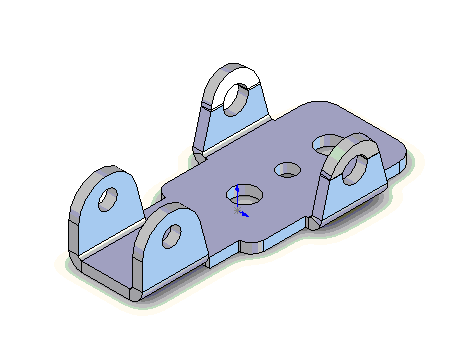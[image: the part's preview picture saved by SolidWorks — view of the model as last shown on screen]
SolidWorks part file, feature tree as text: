
SOLIDWORKS PART (.sldprt)
format: sldprt  version: not decoded by parser v0  size: 605,184 bytes
history: native  units: mm
features: sketch x7, cut_extrude x3, fillet x2, extrude x1, shell x1, sheet_metal_op x1 (+11 scaffold rows collapsed)
feature tree (26):
  scaffold x11  (default folders/planes/origin — collapsed)
  sketch  "Sketch1"  dims[D1=42.8625mm D2=21.0mm]
  extrude  "Extrude1"  Depth=11.1125mm
  sketch  "Sketch2"  dims[c1.D9=2.0mm c1.D10=1.0mm c1.D11=4.2mm c1.D12=4.1mm c1.D13=4.1mm c1.D7=3.0mm c1.D1=2.5mm c1.D2=4.5mm c1.D3=2.0mm c2.D3=95.0deg c2.D4=~2.645638mm c3.D4=100.0deg c3.D5=~2.839605mm c4.D5=100.0deg c4.D6=11.0mm c4.D7=7.9mm c4.D8=16.0mm c4.D12=14.0mm c4.D13=6.2mm c5.D5=6.5405mm c5.D14=7.0mm]
  cut_extrude  "Cut-Extrude1"  [1 undecoded]
  fillet  "Fillet1"  Radius=0.25mm
  sketch  "Sketch3"  dims[c1.D2=~3.061489mm c1.D3=~3.061489mm c1.D4=~3.061489mm c1.D5=8.0mm c1.D6=4.1mm c1.D8=3.1mm c2.D4=3.1mm c2.D9=4.1mm c2.D1=1.6mm c2.D2=10.7mm c2.D3=~7.79288mm c3.D2=7.62mm c3.D3=4.7625mm c3.D4=26.0mm c3.D7=~5.455429mm c4.D7=75.0deg c4.D4=~24.912848mm c4.D9=6.7mm c5.D4=25.4mm c5.D3=1.27mm]
  cut_extrude  "Cut-Extrude2"  [1 undecoded]
  sketch  "Sketch6"  dims[c1.D1=1.0mm c1.D2=1.0mm c2.D1=2.0mm c2.D2=3.0mm c2.D3=~2.895126mm c3.D3=100.0deg c3.D4=~2.519283mm c4.D4=100.0deg]
  cut_extrude  "Cut-Extrude3"  Depth=20mm
  fillet  "Fillet2"  Radius=3mm
  shell  "Shell2"  Thickness=1.6mm
  sheet_metal_op  "Sheet-Metal2"  Thickness=1.6mm
  sketch  "Sharp-Sketch2"  dims[c1.SharpBend5=0.0 c1.D1=0.0mm c1.D4=90.0deg c1.D5=4.0 c1.D8=0.0mm c1.D9=0.0mm c1.SharpBend6=0.0 c2.D1=0.0mm c2.D4=90.0deg c2.D5=3.0 c2.D8=0.0mm c2.D9=0.0mm c2.SharpBend7=0.0 c3.D1=0.0mm c3.D4=90.0deg c3.D5=2.0 c3.D8=0.0mm c3.D9=0.0mm c4.D1=0.5mm c4.D2=500.0mm c4.D3=0.0mm c5.D2=500.0mm c5.D3=0.0mm c5.D4=90.0deg c5.D5=1.0 c5.D8=0.0mm c5.D9=0.0mm]
  sketch  "Flat-Sketch2"  dims[c1.D1=1.0mm c1.D2=1.0mm c2.D1=15.5mm c2.D2=15.5mm c2.FlatBend1=0.0 c3.D1=0.5mm c3.D2=500.0mm c3.D3=0.0mm c3.D4=7.0deg c3.D5=5.0 c3.D8=0.0mm c3.D9=0.0mm c3.FlatBend2=0.0 c4.D1=0.5mm c4.D2=500.0mm c4.D3=0.0mm c4.D4=7.0deg c4.D5=6.0 c4.D8=0.0mm c4.D9=0.0mm c5.D1=0.5mm c5.D2=500.0mm c5.D3=0.0mm]
  sketch  "Sketch8"
decode coverage: 12 of 15 modeling features carry decoded parameters
note: ~ marks probable driven/reference dimensions
note: 2 parameter values undecoded
note: suppression state not decoded; provenance and decode notes live in map.json
